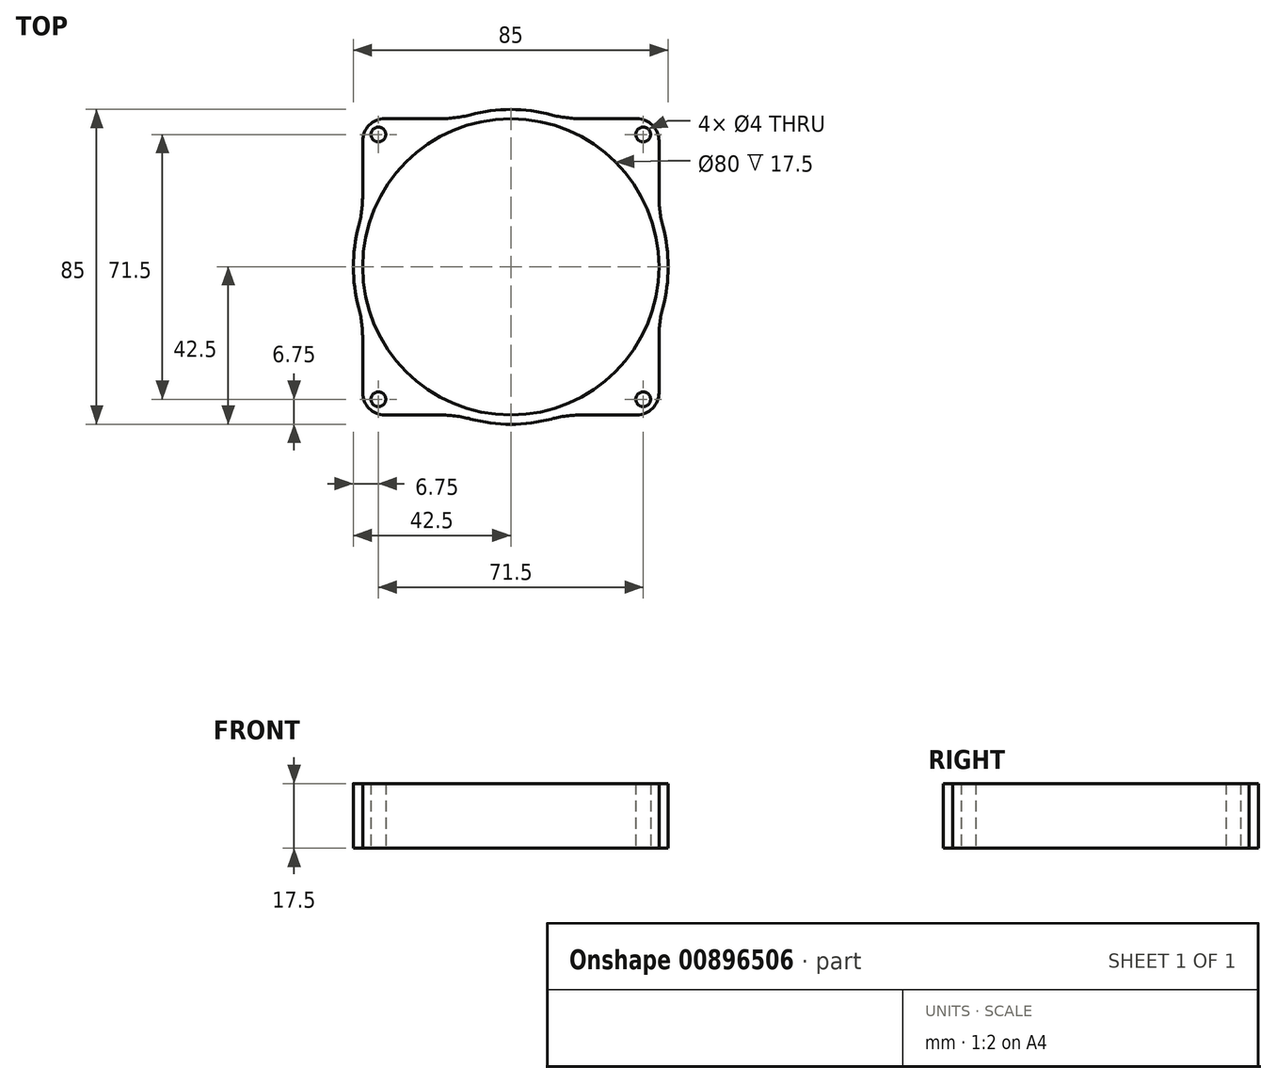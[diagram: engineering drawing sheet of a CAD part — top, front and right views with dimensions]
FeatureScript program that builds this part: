
annotation { "Feature Type Name" : "Feature", "Feature Type Description" : "" }
export const myFeature = defineFeature(function(context is Context, id is Id, definition is map)
    precondition{}
    {
        {
            var Q0;
            Q0=qCreatedBy(makeId("Top.planeOp"),FACE);
            var sketch = newSketch(context, id + "F0", { "sketchPlane" : qUnion([Q0])});
            skLineSegment(sketch, "E0.bottom", {"start": v(35.75, 35.75) * mm, "end": v(-35.75, 35.75) * mm, "construction": true});
            skLineSegment(sketch, "E0.top", {"start": v(35.75, -35.75) * mm, "end": v(-35.75, -35.75) * mm, "construction": true});
            skLineSegment(sketch, "E0.left", {"start": v(35.75, 35.75) * mm, "end": v(35.75, -35.75) * mm, "construction": true});
            skLineSegment(sketch, "E0.right", {"start": v(-35.75, 35.75) * mm, "end": v(-35.75, -35.75) * mm, "construction": true});
            skPoint(sketch, "E0.middle", {"position": v(0, 0) * mm});
            skCircle(sketch, "E1", {"center": v(35.75, 35.75) * mm, "radius": 2 * mm});
            skCircle(sketch, "E2", {"center": v(-35.75, 35.75) * mm, "radius": 2 * mm});
            skCircle(sketch, "E3", {"center": v(-35.75, -35.75) * mm, "radius": 2 * mm});
            skCircle(sketch, "E4", {"center": v(35.75, -35.75) * mm, "radius": 2 * mm});
            skLineSegment(sketch, "E5.bottom", {"start": v(40, 40) * mm, "end": v(-40, 40) * mm});
            skLineSegment(sketch, "E5.top", {"start": v(40, -40) * mm, "end": v(-40, -40) * mm});
            skLineSegment(sketch, "E5.left", {"start": v(40, 40) * mm, "end": v(40, -40) * mm});
            skLineSegment(sketch, "E5.right", {"start": v(-40, 40) * mm, "end": v(-40, -40) * mm});
            skCircle(sketch, "E6", {"center": v(0, 0) * mm, "radius": 40 * mm});
            skCircle(sketch, "E7", {"center": v(0, 0) * mm, "radius": 42.5 * mm});
            skSolve(sketch);
        }
        {
            var Q0;
            Q0 = qSketchRegion(id + "F0", true);
            extrude(context, id + "F1", {"entities" : qUnion([Q0]), "depth" : 17.5 * mm, "offsetDistance" : 25 * mm});
        }
        {
            var Q0;
            Q0=makeQuery(id+"F1.opExtrude","SWEPT_EDGE",EDGE,{"disambiguationData":[OSD([sQuery(id+"F0.wireOp",EDGE,"E5.top"),sQuery(id+"F0.wireOp",EDGE,"E5.right")])]});
            var Q1;
            Q1=makeQuery(id+"F1.opExtrude","SWEPT_EDGE",EDGE,{"disambiguationData":[OSD([sQuery(id+"F0.wireOp",EDGE,"E5.top"),sQuery(id+"F0.wireOp",EDGE,"E5.left")])]});
            var Q2;
            Q2=makeQuery(id+"F1.opExtrude","SWEPT_EDGE",EDGE,{"disambiguationData":[OSD([sQuery(id+"F0.wireOp",EDGE,"E5.bottom"),sQuery(id+"F0.wireOp",EDGE,"E5.right")])]});
            var Q3;
            Q3=makeQuery(id+"F1.opExtrude","SWEPT_EDGE",EDGE,{"disambiguationData":[OSD([sQuery(id+"F0.wireOp",EDGE,"E5.bottom"),sQuery(id+"F0.wireOp",EDGE,"E5.left")])]});
            fillet(context, id + "F2", {"entities" : qUnion([Q0, Q1, Q2, Q3]), "tangentPropagation" : true, "radius" : 6 * mm, "defaultsChanged" : true, "vertexSettings" : [], "allowEdgeOverflow" : false});
        }
        {
            var Q0;
            {var subQ0=sQuery(id+"F0.wireOp",EDGE,"E7");var subQ1=sQuery(id+"F0.wireOp",EDGE,"E5.right");Q0=makeQuery(id+"F1.opExtrude","SWEPT_EDGE",EDGE,{"disambiguationData":[OSD([subQ1,subQ0]),TDD([makeQuery(id+"F0.imprint","INTERSECT",VERTEX,{"disambiguationData":[OD(0.0)],"derivedFrom":[subQ1,subQ0]})])]});}
            var Q1;
            {var subQ0=sQuery(id+"F0.wireOp",EDGE,"E7");var subQ1=sQuery(id+"F0.wireOp",EDGE,"E5.right");Q1=makeQuery(id+"F1.opExtrude","SWEPT_EDGE",EDGE,{"disambiguationData":[OSD([subQ1,subQ0]),TDD([makeQuery(id+"F0.imprint","INTERSECT",VERTEX,{"disambiguationData":[OD(1.0)],"derivedFrom":[subQ1,subQ0]})])]});}
            var Q2;
            {var subQ0=sQuery(id+"F0.wireOp",EDGE,"E7");var subQ1=sQuery(id+"F0.wireOp",EDGE,"E5.top");Q2=makeQuery(id+"F1.opExtrude","SWEPT_EDGE",EDGE,{"disambiguationData":[OSD([subQ1,subQ0]),TDD([makeQuery(id+"F0.imprint","INTERSECT",VERTEX,{"disambiguationData":[OD(1.0)],"derivedFrom":[subQ1,subQ0]})])]});}
            var Q3;
            {var subQ0=sQuery(id+"F0.wireOp",EDGE,"E7");var subQ1=sQuery(id+"F0.wireOp",EDGE,"E5.top");Q3=makeQuery(id+"F1.opExtrude","SWEPT_EDGE",EDGE,{"disambiguationData":[OSD([subQ1,subQ0]),TDD([makeQuery(id+"F0.imprint","INTERSECT",VERTEX,{"disambiguationData":[OD(0.0)],"derivedFrom":[subQ1,subQ0]})])]});}
            var Q4;
            {var subQ0=sQuery(id+"F0.wireOp",EDGE,"E7");var subQ1=sQuery(id+"F0.wireOp",EDGE,"E5.left");Q4=makeQuery(id+"F1.opExtrude","SWEPT_EDGE",EDGE,{"disambiguationData":[OSD([subQ1,subQ0]),TDD([makeQuery(id+"F0.imprint","INTERSECT",VERTEX,{"disambiguationData":[OD(1.0)],"derivedFrom":[subQ1,subQ0]})])]});}
            var Q5;
            {var subQ0=sQuery(id+"F0.wireOp",EDGE,"E7");var subQ1=sQuery(id+"F0.wireOp",EDGE,"E5.left");Q5=makeQuery(id+"F1.opExtrude","SWEPT_EDGE",EDGE,{"disambiguationData":[OSD([subQ1,subQ0]),TDD([makeQuery(id+"F0.imprint","INTERSECT",VERTEX,{"disambiguationData":[OD(0.0)],"derivedFrom":[subQ1,subQ0]})])]});}
            var Q6;
            {var subQ0=sQuery(id+"F0.wireOp",EDGE,"E7");var subQ1=sQuery(id+"F0.wireOp",EDGE,"E5.bottom");Q6=makeQuery(id+"F1.opExtrude","SWEPT_EDGE",EDGE,{"disambiguationData":[OSD([subQ1,subQ0]),TDD([makeQuery(id+"F0.imprint","INTERSECT",VERTEX,{"disambiguationData":[OD(0.0)],"derivedFrom":[subQ1,subQ0]})])]});}
            var Q7;
            {var subQ0=sQuery(id+"F0.wireOp",EDGE,"E7");var subQ1=sQuery(id+"F0.wireOp",EDGE,"E5.bottom");Q7=makeQuery(id+"F1.opExtrude","SWEPT_EDGE",EDGE,{"disambiguationData":[OSD([subQ1,subQ0]),TDD([makeQuery(id+"F0.imprint","INTERSECT",VERTEX,{"disambiguationData":[OD(1.0)],"derivedFrom":[subQ1,subQ0]})])]});}
            fillet(context, id + "F3", {"entities" : qUnion([Q0, Q1, Q2, Q3, Q4, Q5, Q6, Q7]), "tangentPropagation" : true, "radius" : 32 * mm, "defaultsChanged" : true, "vertexSettings" : [], "allowEdgeOverflow" : false});
        }
    });
